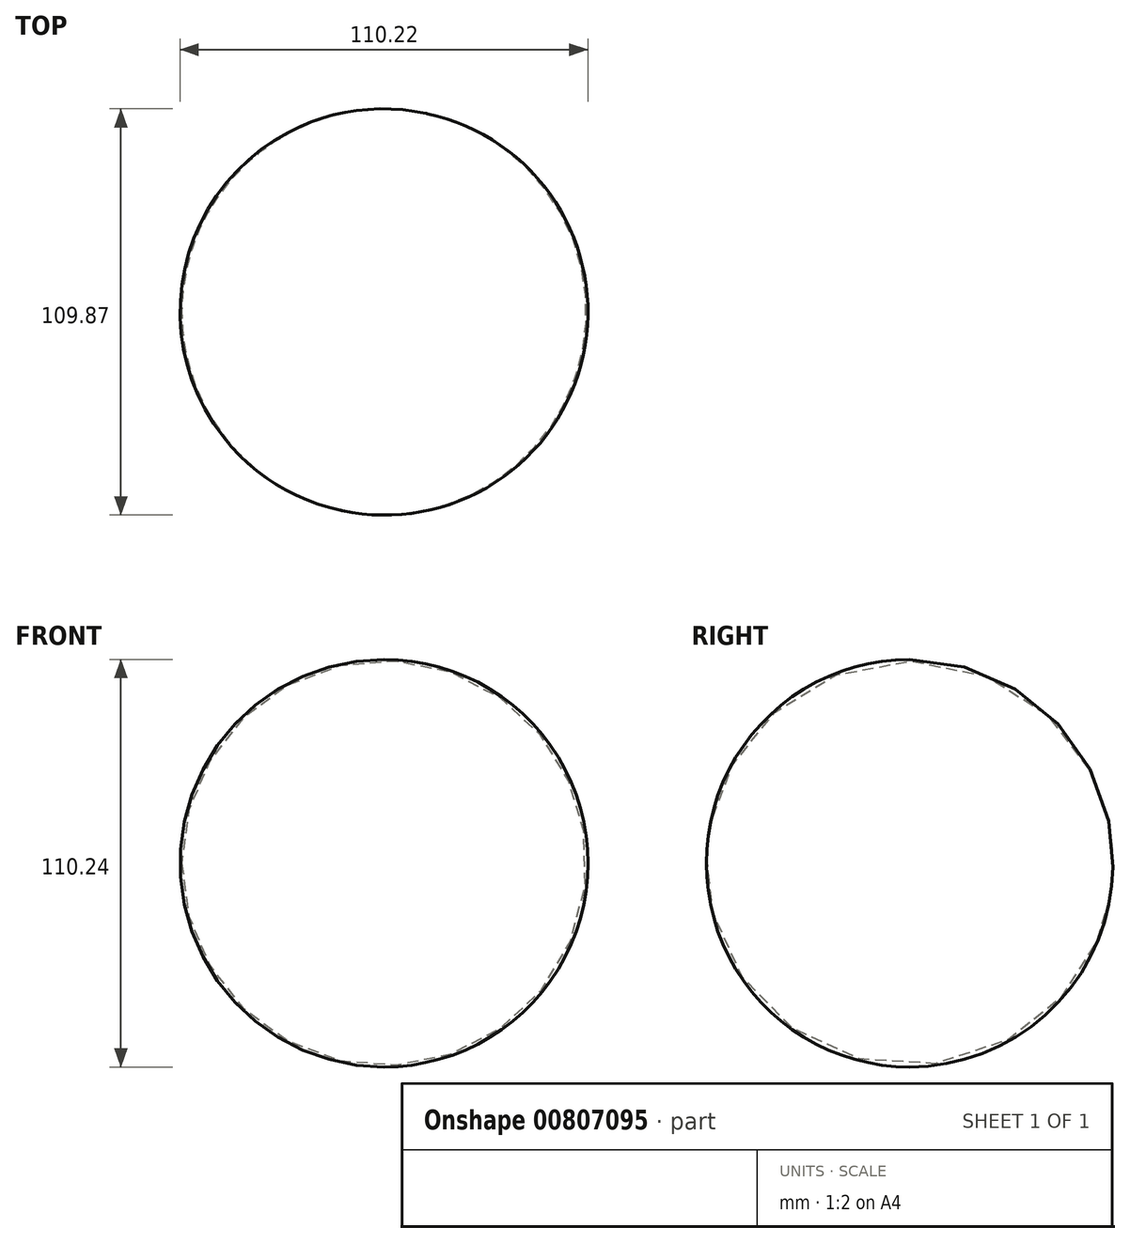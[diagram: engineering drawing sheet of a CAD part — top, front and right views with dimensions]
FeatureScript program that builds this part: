
annotation { "Feature Type Name" : "Feature", "Feature Type Description" : "" }
export const myFeature = defineFeature(function(context is Context, id is Id, definition is map)
    precondition{}
    {
        {
            var Q0;
            Q0=qCreatedBy(makeId("Top.planeOp"),FACE);
            var sketch = newSketch(context, id + "F0", { "sketchPlane" : qUnion([Q0])});
            skCircle(sketch, "E0", {"center": v(-46.63, 28.95) * mm, "radius": 54.9 * mm});
            skSolve(sketch);
        }
        {
            var Q0;
            Q0=makeQuery(id+"F0.imprint","IMPRINT",FACE,{"disambiguationData":[TD([[makeQuery(id+"F0.imprint","IMPRINT",EDGE,{"derivedFrom":sQuery(id+"F0.wireOp",EDGE,"E0")}),1.0]])]});
            var sketch = newSketch(context, id + "F1", { "sketchPlane" : qUnion([Q0])});
            skLineSegment(sketch, "E1", {"start": v(-57.99, -24.86) * mm, "end": v(-34.69, 83.38) * mm});
            skSolve(sketch);
        }
        {
            var Q0;
            {var subQ0=sQuery(id+"F1.wireOp",EDGE,"E1");var subQ1=makeQuery(id+"F0.imprint","IMPRINT",EDGE,{"derivedFrom":sQuery(id+"F0.wireOp",EDGE,"E0")});var subQ2=makeQuery(id+"F1.imprint","INTERSECT",VERTEX,{"disambiguationData":[OD(0.0)],"derivedFrom":[subQ1,subQ0]});Q0=makeQuery(id+"F1.imprint","IMPRINT",FACE,{"disambiguationData":[TD([[makeQuery(id+"F1.imprint","IMPRINT",EDGE,{"disambiguationData":[TD([[subQ2,-1.0]])],"derivedFrom":subQ0}),1.0]])]});}
            var Q1;
            Q1=sQuery(id+"F1.wireOp",EDGE,"E1");
            revolve(context, id + "F2", {"surfaceOperationType" : NewSurfaceOperationType.NEW, "entities" : qUnion([Q0]), "axis" : qUnion([Q1]), "revolveType" : RevolveType.FULL});
        }
    });
